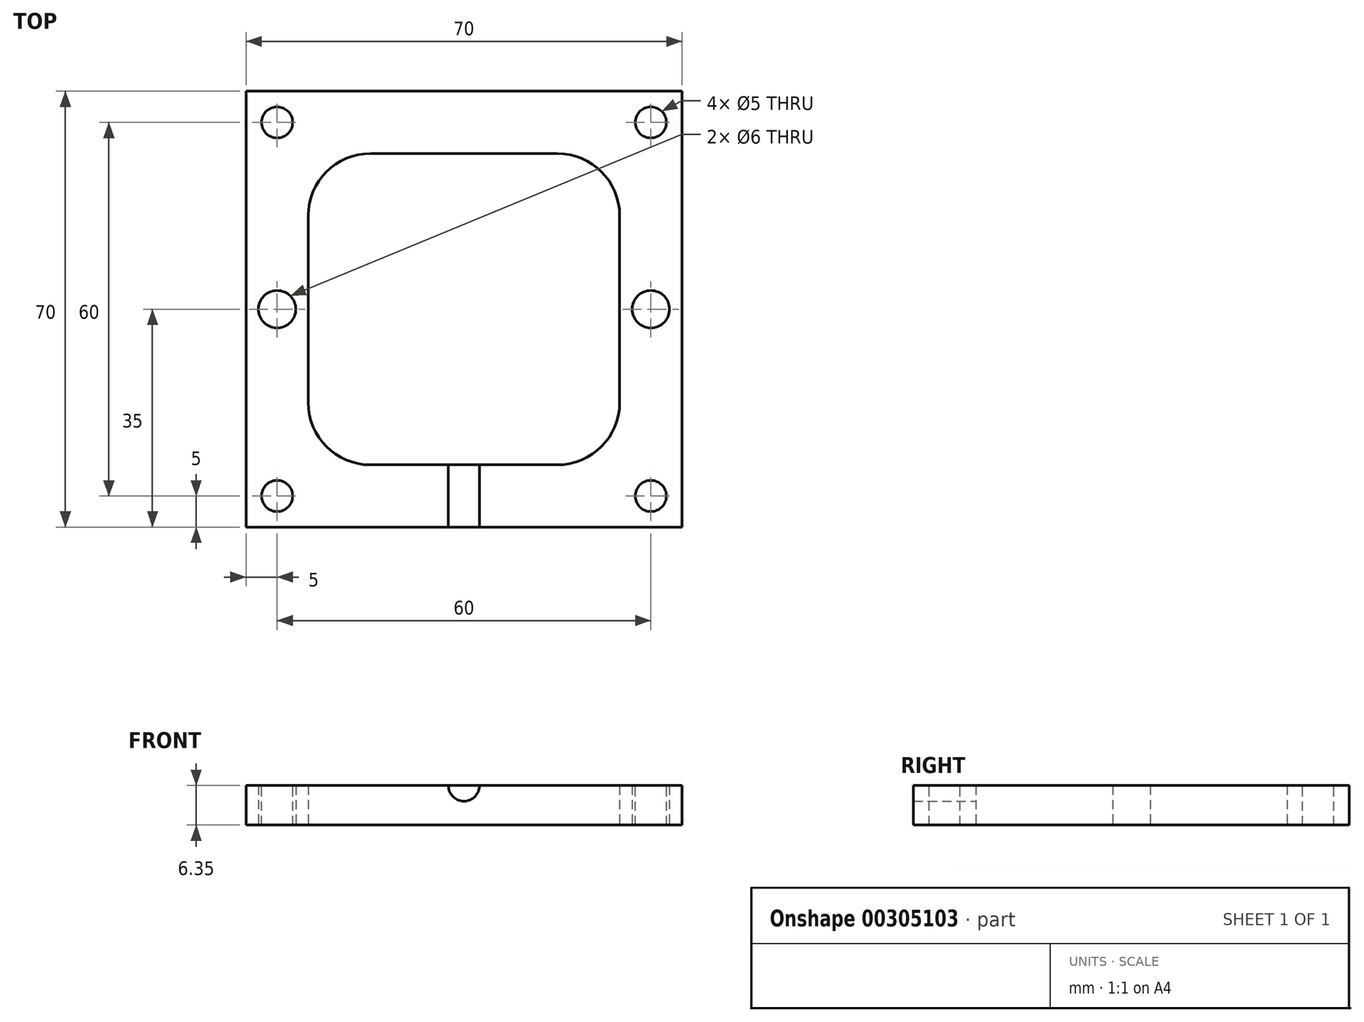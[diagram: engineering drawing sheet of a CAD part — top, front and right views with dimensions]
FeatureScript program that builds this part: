
annotation { "Feature Type Name" : "Feature", "Feature Type Description" : "" }
export const myFeature = defineFeature(function(context is Context, id is Id, definition is map)
    precondition{}
    {
        {
            var Q0;
            Q0=qCreatedBy(makeId("Top.planeOp"),FACE);
            var sketch = newSketch(context, id + "F0", { "sketchPlane" : qUnion([Q0])});
            skLineSegment(sketch, "E0.bottom", {"start": v(35, -35) * mm, "end": v(-35, -35) * mm});
            skLineSegment(sketch, "E0.top", {"start": v(35, 35) * mm, "end": v(-35, 35) * mm});
            skLineSegment(sketch, "E0.left", {"start": v(35, -35) * mm, "end": v(35, 35) * mm});
            skLineSegment(sketch, "E0.right", {"start": v(-35, -35) * mm, "end": v(-35, 35) * mm});
            skPoint(sketch, "E0.middle", {"position": v(0, 0) * mm});
            skLineSegment(sketch, "E1.bottom", {"start": v(-15, 25) * mm, "end": v(15, 25) * mm});
            skLineSegment(sketch, "E1.top", {"start": v(-15, -25) * mm, "end": v(15, -25) * mm});
            skLineSegment(sketch, "E1.left", {"start": v(-25, 15) * mm, "end": v(-25, -15) * mm});
            skLineSegment(sketch, "E1.right", {"start": v(25, 15) * mm, "end": v(25, -15) * mm});
            skLineSegment(sketch, "E2", {"start": v(-35, 0) * mm, "end": v(35, 0) * mm});
            skCircle(sketch, "E3", {"center": v(-30, 0) * mm, "radius": 3 * mm});
            skCircle(sketch, "E4", {"center": v(30, 0) * mm, "radius": 3 * mm});
            skPoint(sketch, "E5.visualSharp", {"position": v(-25, 25) * mm});
            skArc(sketch, "E5.filletArc", {"start": v(-15, 25) * mm, "mid": v(-22.07, 22.07) * mm, "end": v(-25, 15) * mm});
            skPoint(sketch, "E6.visualSharp", {"position": v(-25, -25) * mm});
            skArc(sketch, "E6.filletArc", {"start": v(-25, -15) * mm, "mid": v(-22.07, -22.07) * mm, "end": v(-15, -25) * mm});
            skPoint(sketch, "E7.visualSharp", {"position": v(25, -25) * mm});
            skArc(sketch, "E7.filletArc", {"start": v(15, -25) * mm, "mid": v(22.07, -22.07) * mm, "end": v(25, -15) * mm});
            skPoint(sketch, "E8.visualSharp", {"position": v(25, 25) * mm});
            skArc(sketch, "E8.filletArc", {"start": v(25, 15) * mm, "mid": v(22.07, 22.07) * mm, "end": v(15, 25) * mm});
            skSolve(sketch);
        }
        {
            var Q0;
            {var subQ14=sQuery(id+"F0.wireOp",EDGE,"E0.bottom");Q0=makeQuery(id+"F0.imprint","IMPRINT",FACE,{"disambiguationData":[TD([[makeQuery(id+"F0.imprint","IMPRINT",EDGE,{"derivedFrom":subQ14}),-1.0]])]});}
            var Q1;
            {var subQ15=sQuery(id+"F0.wireOp",EDGE,"E0.top");Q1=makeQuery(id+"F0.imprint","IMPRINT",FACE,{"disambiguationData":[TD([[makeQuery(id+"F0.imprint","IMPRINT",EDGE,{"derivedFrom":subQ15}),1.0]])]});}
            extrude(context, id + "F1", {"entities" : qUnion([Q0, Q1]), "depth" : 6.35 * mm});
        }
        {
            var Q0;
            Q0=makeQuery(id+"F1.opExtrude","SWEPT_FACE",FACE,{"disambiguationData":[OSD([sQuery(id+"F0.wireOp",EDGE,"E0.bottom")])]});
            var sketch = newSketch(context, id + "F2", { "sketchPlane" : qUnion([Q0])});
            skPoint(sketch, "E9", {"position": v(0, 6.35) * mm});
            skSolve(sketch);
        }
        {
            var Q0;
            Q0=sQuery(id+"F2.wireOp",VERTEX,"E9");
            var Q1;
            Q1=makeQuery(id+"F1.opExtrude","SWEPT_BODY",BODY,{"disambiguationData":[OSD([sQuery(id+"F0.wireOp",EDGE,"E0.bottom"),sQuery(id+"F0.wireOp",EDGE,"E0.top"),sQuery(id+"F0.wireOp",EDGE,"E0.left"),sQuery(id+"F0.wireOp",EDGE,"E0.right"),sQuery(id+"F0.wireOp",EDGE,"E1.bottom"),sQuery(id+"F0.wireOp",EDGE,"E1.top"),sQuery(id+"F0.wireOp",EDGE,"E1.left"),sQuery(id+"F0.wireOp",EDGE,"E1.right"),sQuery(id+"F0.wireOp",EDGE,"E3"),sQuery(id+"F0.wireOp",EDGE,"E4"),sQuery(id+"F0.wireOp",EDGE,"E5.filletArc"),sQuery(id+"F0.wireOp",EDGE,"E6.filletArc"),sQuery(id+"F0.wireOp",EDGE,"E7.filletArc"),sQuery(id+"F0.wireOp",EDGE,"E8.filletArc")])]});
            hole(context, id + "F3", {"style" : HoleStyle.SIMPLE, "endStyle" : HoleEndStyle.BLIND, "standardTappedOrClearance" : lookupTablePath({ "standard" : "ISO", "size" : "5", "type" : "Drilled" }), "standardBlindInLast" : lookupTablePath({ "standard" : "ISO", "size" : "5", "type" : "Drilled" }), "holeDiameter" : 5 * mm, "holeDepth" : 14.4 * mm, "isTappedThrough" : true, "tappedDepth" : 12 * mm, "tapClearance" : 3, "locations" : qUnion([Q0]), "scope" : qUnion([Q1]), "startStyle" : HoleStartStyle.PART});
        }
        {
            var Q0;
            Q0=makeQuery(id+"F1.opExtrude","CAP_FACE",FACE,{"disambiguationData":[OSD([sQuery(id+"F0.wireOp",EDGE,"E0.bottom"),sQuery(id+"F0.wireOp",EDGE,"E0.top"),sQuery(id+"F0.wireOp",EDGE,"E0.left"),sQuery(id+"F0.wireOp",EDGE,"E0.right"),sQuery(id+"F0.wireOp",EDGE,"E1.bottom"),sQuery(id+"F0.wireOp",EDGE,"E1.top"),sQuery(id+"F0.wireOp",EDGE,"E1.left"),sQuery(id+"F0.wireOp",EDGE,"E1.right"),sQuery(id+"F0.wireOp",EDGE,"E3"),sQuery(id+"F0.wireOp",EDGE,"E4"),sQuery(id+"F0.wireOp",EDGE,"E5.filletArc"),sQuery(id+"F0.wireOp",EDGE,"E6.filletArc"),sQuery(id+"F0.wireOp",EDGE,"E7.filletArc"),sQuery(id+"F0.wireOp",EDGE,"E8.filletArc")])],"isStart":true});
            var sketch = newSketch(context, id + "F4", { "sketchPlane" : qUnion([Q0])});
            skLineSegment(sketch, "E10.bottom", {"start": v(-30, 30) * mm, "end": v(30, 30) * mm});
            skLineSegment(sketch, "E10.top", {"start": v(-30, -30) * mm, "end": v(30, -30) * mm});
            skLineSegment(sketch, "E10.left", {"start": v(-30, 30) * mm, "end": v(-30, -30) * mm});
            skLineSegment(sketch, "E10.right", {"start": v(30, 30) * mm, "end": v(30, -30) * mm});
            skPoint(sketch, "E10.middle", {"position": v(0, 0) * mm});
            skSolve(sketch);
        }
        {
            var Q0;
            Q0=sQuery(id+"F4.wireOp",VERTEX,"E10.left.start");
            var Q1;
            Q1=sQuery(id+"F4.wireOp",VERTEX,"E10.right.start");
            var Q2;
            Q2=sQuery(id+"F4.wireOp",VERTEX,"E10.top.end");
            var Q3;
            Q3=sQuery(id+"F4.wireOp",VERTEX,"E10.left.end");
            var Q4;
            Q4=makeQuery(id+"F1.opExtrude","SWEPT_BODY",BODY,{"disambiguationData":[OSD([sQuery(id+"F0.wireOp",EDGE,"E0.bottom"),sQuery(id+"F0.wireOp",EDGE,"E0.top"),sQuery(id+"F0.wireOp",EDGE,"E0.left"),sQuery(id+"F0.wireOp",EDGE,"E0.right"),sQuery(id+"F0.wireOp",EDGE,"E1.bottom"),sQuery(id+"F0.wireOp",EDGE,"E1.top"),sQuery(id+"F0.wireOp",EDGE,"E1.left"),sQuery(id+"F0.wireOp",EDGE,"E1.right"),sQuery(id+"F0.wireOp",EDGE,"E3"),sQuery(id+"F0.wireOp",EDGE,"E4"),sQuery(id+"F0.wireOp",EDGE,"E5.filletArc"),sQuery(id+"F0.wireOp",EDGE,"E6.filletArc"),sQuery(id+"F0.wireOp",EDGE,"E7.filletArc"),sQuery(id+"F0.wireOp",EDGE,"E8.filletArc")])]});
            hole(context, id + "F5", {"style" : HoleStyle.SIMPLE, "endStyle" : HoleEndStyle.BLIND, "standardTappedOrClearance" : lookupTablePath({ "standard" : "ISO", "engagement" : "75%", "pitch" : "1 mm", "size" : "M6", "type" : "Tapped" }), "standardBlindInLast" : lookupTablePath({ "standard" : "ISO", "engagement" : "75%", "pitch" : "1 mm", "size" : "M6", "type" : "Tapped" }), "holeDiameter" : 5 * mm, "showTappedDepth" : true, "holeDepth" : 15 * mm, "isTappedThrough" : true, "tappedDepth" : 12 * mm, "tapClearance" : 3, "locations" : qUnion([Q0, Q1, Q2, Q3]), "scope" : qUnion([Q4]), "majorDiameter" : 6 * mm, "startStyle" : HoleStartStyle.SKETCH});
        }
    });
